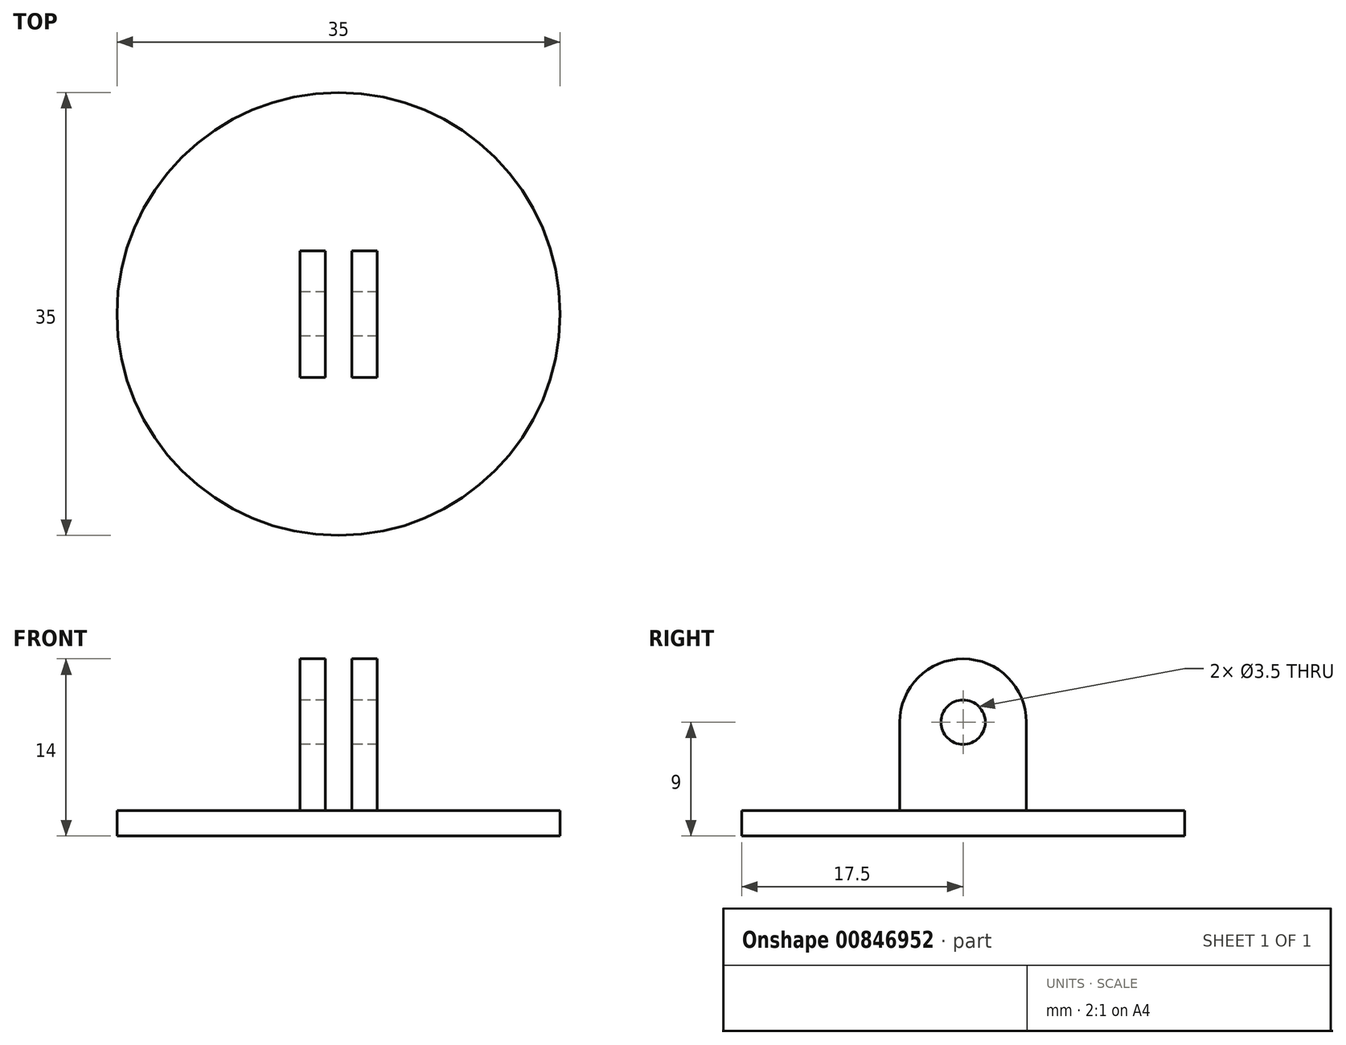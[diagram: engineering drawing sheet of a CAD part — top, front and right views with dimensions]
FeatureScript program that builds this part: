
annotation { "Feature Type Name" : "Feature", "Feature Type Description" : "" }
export const myFeature = defineFeature(function(context is Context, id is Id, definition is map)
    precondition{}
    {
        {
            var Q0;
            Q0=qCreatedBy(makeId("Top.planeOp"),FACE);
            var sketch = newSketch(context, id + "F0", { "sketchPlane" : qUnion([Q0])});
            skLineSegment(sketch, "E0", {"start": v(0, 16.03) * mm, "end": v(0, -20.56) * mm, "construction": true});
            skLineSegment(sketch, "E1", {"start": v(-21.97, 0) * mm, "end": v(21.43, 0) * mm, "construction": true});
            skCircle(sketch, "E2", {"center": v(0, 0) * mm, "radius": 17.5 * mm});
            skLineSegment(sketch, "E3", {"start": v(-3.05, 0) * mm, "end": v(-3.05, 5) * mm});
            skLineSegment(sketch, "E4", {"start": v(-3.05, 5) * mm, "end": v(-1.05, 5) * mm});
            skLineSegment(sketch, "E5", {"start": v(-1.05, 5) * mm, "end": v(-1.05, 0) * mm});
            skLineSegment(sketch, "E6.MirrorCS", {"start": v(-3.05, 0) * mm, "end": v(-3.05, -5) * mm});
            skLineSegment(sketch, "E7.MirrorCS", {"start": v(-3.05, -5) * mm, "end": v(-1.05, -5) * mm});
            skLineSegment(sketch, "E8.MirrorCS", {"start": v(-1.05, -5) * mm, "end": v(-1.05, 0) * mm});
            skLineSegment(sketch, "E9.MirrorCS", {"start": v(3.05, 5) * mm, "end": v(1.05, 5) * mm});
            skLineSegment(sketch, "E10.MirrorCS", {"start": v(3.05, 0) * mm, "end": v(3.05, 5) * mm});
            skLineSegment(sketch, "E11.MirrorCS", {"start": v(3.05, 0) * mm, "end": v(3.05, -5) * mm});
            skLineSegment(sketch, "E12.MirrorCS", {"start": v(3.05, -5) * mm, "end": v(1.05, -5) * mm});
            skLineSegment(sketch, "E13.MirrorCS", {"start": v(1.05, -5) * mm, "end": v(1.05, 0) * mm});
            skLineSegment(sketch, "E14.MirrorCS", {"start": v(1.05, 5) * mm, "end": v(1.05, 0) * mm});
            skSolve(sketch);
        }
        {
            var Q0;
            Q0=makeQuery(id+"F0.imprint","IMPRINT",FACE,{"disambiguationData":[TD([[makeQuery(id+"F0.imprint","IMPRINT",EDGE,{"derivedFrom":sQuery(id+"F0.wireOp",EDGE,"E3")}),-1.0]])]});
            var Q1;
            Q1=makeQuery(id+"F0.imprint","IMPRINT",FACE,{"disambiguationData":[TD([[makeQuery(id+"F0.imprint","IMPRINT",EDGE,{"derivedFrom":sQuery(id+"F0.wireOp",EDGE,"E9.MirrorCS")}),1.0]])]});
            extrude(context, id + "F1", {"entities" : qUnion([Q0, Q1]), "depth" : 12 * mm, "offsetDistance" : 25 * mm});
        }
        {
            var Q0;
            Q0=makeQuery(id+"F0.imprint","IMPRINT",FACE,{"disambiguationData":[TD([[makeQuery(id+"F0.imprint","IMPRINT",EDGE,{"derivedFrom":sQuery(id+"F0.wireOp",EDGE,"E2")}),1.0]])]});
            var Q1;
            Q1=makeQuery(id+"F0.imprint","IMPRINT",FACE,{"disambiguationData":[TD([[makeQuery(id+"F0.imprint","IMPRINT",EDGE,{"derivedFrom":sQuery(id+"F0.wireOp",EDGE,"E3")}),-1.0]])]});
            var Q2;
            Q2=makeQuery(id+"F0.imprint","IMPRINT",FACE,{"disambiguationData":[TD([[makeQuery(id+"F0.imprint","IMPRINT",EDGE,{"derivedFrom":sQuery(id+"F0.wireOp",EDGE,"E9.MirrorCS")}),1.0]])]});
            extrude(context, id + "F2", {"entities" : qUnion([Q0, Q1, Q2]), "depth" : -2 * mm, "offsetDistance" : 25 * mm});
        }
        {
            var Q0;
            Q0=makeQuery(id+"F1.opExtrude","SWEPT_FACE",FACE,{"disambiguationData":[OSD([sQuery(id+"F0.wireOp",EDGE,"E3"),sQuery(id+"F0.wireOp",EDGE,"E6.MirrorCS")])]});
            var sketch = newSketch(context, id + "F3", { "sketchPlane" : qUnion([Q0])});
            skLineSegment(sketch, "E15", {"start": v(0, 12) * mm, "end": v(0, 3.7) * mm, "construction": true});
            skLineSegment(sketch, "E16", {"start": v(-5, 12) * mm, "end": v(5, 12) * mm, "construction": true});
            skLineSegment(sketch, "E17", {"start": v(0, 12) * mm, "end": v(0, 7) * mm, "construction": true});
            skCircle(sketch, "E18", {"center": v(0, 7) * mm, "radius": 5 * mm});
            skCircle(sketch, "E19", {"center": v(0, 7) * mm, "radius": 1.75 * mm});
            skSolve(sketch);
        }
        {
            var Q0;
            {var subQ0=sQuery(id+"F3.wireOp",EDGE,"E18");var subQ1=sQuery(id+"F0.wireOp",EDGE,"E3");var subQ2=makeQuery(id+"F1.opExtrude","CAP_EDGE",EDGE,{"disambiguationData":[OSD([subQ1,sQuery(id+"F0.wireOp",EDGE,"E6.MirrorCS")])],"isStart":false});var subQ3=makeQuery(id+"F3.imprint","INTERSECT",VERTEX,{"derivedFrom":[subQ2,subQ0]});Q0=makeQuery(id+"F3.imprint","IMPRINT",FACE,{"disambiguationData":[TD([[makeQuery(id+"F3.imprint","IMPRINT",EDGE,{"disambiguationData":[TD([[subQ3,-1.0]])],"derivedFrom":subQ0}),-1.0]])]});}
            var Q1;
            Q1=makeQuery(id+"F3.imprint","IMPRINT",FACE,{"disambiguationData":[TD([[makeQuery(id+"F3.imprint","IMPRINT",EDGE,{"derivedFrom":sQuery(id+"F3.wireOp",EDGE,"E19")}),1.0]])]});
            var Q2;
            {var subQ0=sQuery(id+"F3.wireOp",EDGE,"E18");var subQ1=sQuery(id+"F0.wireOp",EDGE,"E6.MirrorCS");var subQ2=makeQuery(id+"F1.opExtrude","CAP_EDGE",EDGE,{"disambiguationData":[OSD([sQuery(id+"F0.wireOp",EDGE,"E3"),subQ1])],"isStart":false});var subQ3=makeQuery(id+"F3.imprint","INTERSECT",VERTEX,{"derivedFrom":[subQ2,subQ0]});Q2=makeQuery(id+"F3.imprint","IMPRINT",FACE,{"disambiguationData":[TD([[makeQuery(id+"F3.imprint","IMPRINT",EDGE,{"disambiguationData":[TD([[subQ3,1.0]])],"derivedFrom":subQ0}),-1.0]])]});}
            extrude(context, id + "F4", {"entities" : qUnion([Q0, Q1, Q2]), "operationType" : NewBodyOperationType.REMOVE, "oppositeDirection" : true, "depth" : 25 * mm, "offsetDistance" : 25 * mm});
        }
    });
